# Revit family: VLN_VenlomixMedical_A5544_BIM_NL
name_source: partatom
category: Plumbing Fixtures
revit_build: Autodesk Revit MEP 2014 (Build: 20130308_1515(x64)
units: mm (PartAtom-declared; Revit-internal decimal feet)

## types (1)
- A554401-VMIX-MED THERM WASTAFEL 1-G CHR
    Accessories = www.idealstandardnederland.nl
    AreaUnits = millimeters
    Assembly Code = C1030200
    AssetType = Vast
    BIMObjectName = VLN_Venlo_SinkTaps_A5544AA
    BREEAMApproved = No
    BarCode = 4015413325981
    Brand = Venlo
    CWFU = 0
    CodePerformance = EN 817, DIN 4109
    Color = Chroom
    ConnectionType = Sanitair
    Cost = 0 $
    Default Elevation = 800 mm
    Description = Venlo Medical Therm new wastafelthermostaat DN 15. Eengats. Draaibare uitloop. Terugslagklep. Geschikt voor thermische desinfectie. Metalen grepen met permanente rood/blauw markering. Thermostatisch waspatroon. Cartouche met keramische schijven. Temperatuurinstelling met extra temperatuurbegrenzing (kinderveiligheid). Geluidsniveau volgens norm DIN 4109, Groep 1.
    DurationUnit = jaar
    ECA = No
    ExpectedLife = 25
    FaucetFunction = Thermostaatkraan
    FaucetOperation = Tweegreeps
    FaucetType = Wastafelthermostaat
    Features = Wastafelthermostaat DN 15. Eengats. Draaibare uitloop. Terugslagklep. Geschikt voor thermische desinfectie. Metalen grepen met permanente rood/blauw markering. Thermostatisch waspatroon. Cartouche met keramische schijven. Temperatuurinstelling met extra temperatuurbegrenzing (kinderveiligheid). Geluidsniveau volgens norm DIN 4109, Groep 1.
    Finish = Chroom
    HWFU = 0
    IfcExportAs = IfcValveType
    IfcExportType = FAUCET
    InstallationInstructions = http://www.idealstandardnederland.nl
    LinearUnits = millimeters
    ManufacturerURL = www.idealstandardnederland.nl
    Material = Messing
    Model = A5544AA
    ModelNumber = A5544AA
    ModelReference = Venlo Medical Therm new wastafelthermostaat DN 15. Eengats. Draaibare uitloop. Terugslagklep. Geschikt voor thermische desinfectie. Metalen grepen met permanente rood/blauw markering. Thermostatisch waspatroon. Cartouche met keramische schijven. Temperatuurinstelling met extra temperatuurbegrenzing (kinderveiligheid). Geluidsniveau volgens norm DIN 4109, Groep 1.
    NBSDescription = Water supply fittings for sinks
    NBSReference = 45-35-70/345
    Name = SinkTaps_A5544AA_Venlo
    NettWeight = 2.856 kg
    NominalHeight = 291 mm
    NominalLength = 212 mm
    NominalWidth = 196 mm
    ProductInformation = http://www.idealstandardnederland.nl
    Shape = Gesculptuurd
    Size = 196 x 212 x 291 mm
    Space = Internal
    SpareParts = www.idealstandardnederland.nl
    TMV3 = No
    TestPressure = 10 Bar
    URL = www.idealstandardnederland.nl
    Uniclass2015Description = Sink taps
    Uniclass2015Reference = Pr_40_20_87_84
    Uniclass2015Version = Products v1.1
    ValveMechanism = Keramische schijven
    ValveOperation = Tweegreeps
    Version = 1
    VolumeUnits = liter
    WFU = 0
    WRAS = No
    WarrantyDescription = Fabrieksgarantie
    WarrantyDurationParts = 5
    WarrantyDurationUnit = jaar
    WaterEfficientProduct = No
    WorkingPressure = 1-5 bar

## geometry (parser evidence)
native form markers: Sweep x2
no freeform markers — native parametric forms only
